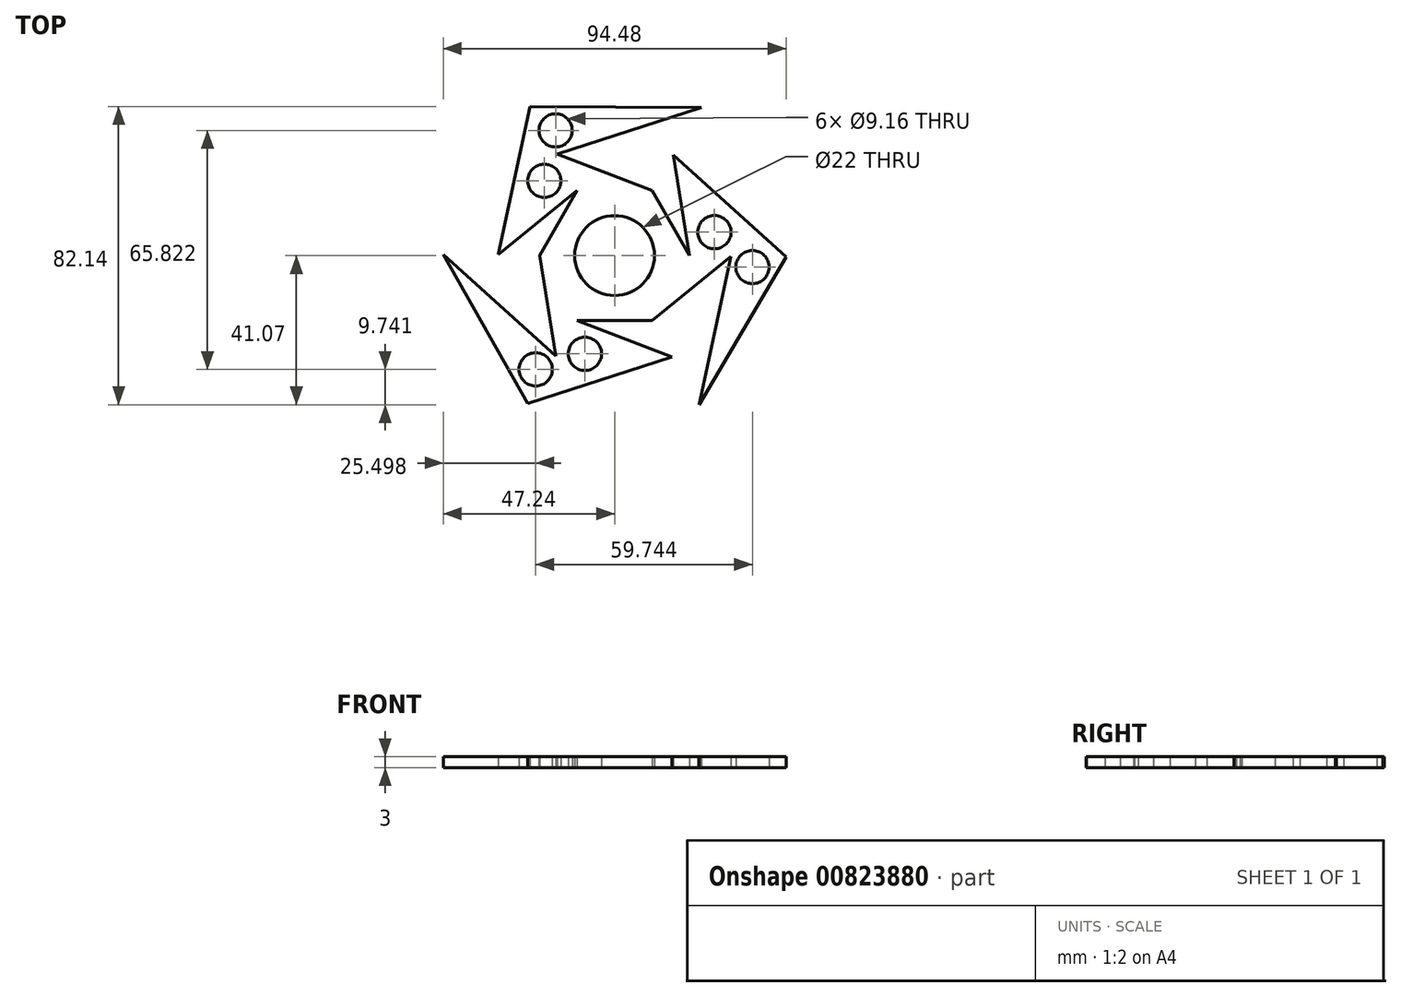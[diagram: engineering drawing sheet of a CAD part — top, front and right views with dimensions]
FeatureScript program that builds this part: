
annotation { "Feature Type Name" : "Feature", "Feature Type Description" : "" }
export const myFeature = defineFeature(function(context is Context, id is Id, definition is map)
    precondition{}
    {
        {
            var Q0;
            Q0=qCreatedBy(makeId("Top.planeOp"),FACE);
            var sketch = newSketch(context, id + "F0", { "sketchPlane" : qUnion([Q0])});
            skLineSegment(sketch, "E0.0", {"start": v(10.34, -17.92) * mm, "end": v(-10.34, -17.92) * mm});
            skPoint(sketch, "E0.0.midPoint", {"position": v(0, -17.92) * mm});
            skPoint(sketch, "E1.0.midPoint", {"position": v(-24.18, -13.74) * mm});
            skLineSegment(sketch, "E2", {"start": v(-20.69, 0) * mm, "end": v(-16.24, -27.7) * mm});
            skLineSegment(sketch, "E3", {"start": v(-10.34, -17.92) * mm, "end": v(15.87, -27.92) * mm});
            skArc(sketch, "E4", {"start": v(-8.4, 0.06) * mm, "mid": v(-8.4, 0.03) * mm, "end": v(-8.4, 0) * mm});
            skPoint(sketch, "E5.0.midPoint", {"position": v(15.87, -27.92) * mm});
            skLineSegment(sketch, "E6.1", {"start": v(-23.9, -40.75) * mm, "end": v(-47.24, 0.32) * mm});
            skPoint(sketch, "E6.0.midPoint", {"position": v(-0.28, -40.91) * mm});
            skLineSegment(sketch, "E7", {"start": v(15.87, -27.92) * mm, "end": v(-23.9, -40.75) * mm});
            skLineSegment(sketch, "E8", {"start": v(-16.24, -27.7) * mm, "end": v(-47.24, 0.32) * mm});
            skCircle(sketch, "E9", {"center": v(-8.17, -27.07) * mm, "radius": 4.58 * mm});
            skCircle(sketch, "E10", {"center": v(-21.74, -31.33) * mm, "radius": 4.58 * mm});
            skLineSegment(sketch, "E11.1.0", {"start": v(10.34, -17.92) * mm, "end": v(32.11, -0.22) * mm});
            skLineSegment(sketch, "E11.1.1", {"start": v(47.24, -0.32) * mm, "end": v(23.34, -41.07) * mm});
            skArc(sketch, "E11.1.2", {"start": v(4.15, -7.3) * mm, "mid": v(4.17, -7.29) * mm, "end": v(4.2, -7.27) * mm});
            skLineSegment(sketch, "E11.1.3", {"start": v(10.34, 17.92) * mm, "end": v(20.69, 0) * mm});
            skPoint(sketch, "E11.1.4", {"position": v(23.99, -14.07) * mm});
            skCircle(sketch, "E11.1.5", {"center": v(27.53, 6.46) * mm, "radius": 4.58 * mm});
            skPoint(sketch, "E11.1.6", {"position": v(16.24, 27.7) * mm});
            skPoint(sketch, "E11.1.7", {"position": v(15.52, 8.96) * mm});
            skCircle(sketch, "E11.1.8", {"center": v(38, -3.16) * mm, "radius": 4.58 * mm});
            skPoint(sketch, "E11.1.9", {"position": v(35.57, 20.22) * mm});
            skLineSegment(sketch, "E11.1.10", {"start": v(16.24, 27.7) * mm, "end": v(47.24, -0.32) * mm});
            skLineSegment(sketch, "E11.1.11", {"start": v(32.11, -0.22) * mm, "end": v(23.34, -41.07) * mm});
            skLineSegment(sketch, "E11.1.12", {"start": v(20.69, 0) * mm, "end": v(16.24, 27.7) * mm});
            skLineSegment(sketch, "E11.2.0", {"start": v(10.34, 17.92) * mm, "end": v(-15.87, 27.92) * mm});
            skLineSegment(sketch, "E11.2.1", {"start": v(-23.34, 41.07) * mm, "end": v(23.9, 40.75) * mm});
            skArc(sketch, "E11.2.2", {"start": v(4.25, 7.24) * mm, "mid": v(4.22, 7.26) * mm, "end": v(4.2, 7.27) * mm});
            skLineSegment(sketch, "E11.2.3", {"start": v(-20.69, 0) * mm, "end": v(-10.34, 17.92) * mm});
            skPoint(sketch, "E11.2.4", {"position": v(0.19, 27.8) * mm});
            skCircle(sketch, "E11.2.5", {"center": v(-19.35, 20.6) * mm, "radius": 4.58 * mm});
            skPoint(sketch, "E11.2.6", {"position": v(-32.11, 0.22) * mm});
            skPoint(sketch, "E11.2.7", {"position": v(-15.52, 8.96) * mm});
            skCircle(sketch, "E11.2.8", {"center": v(-16.26, 34.5) * mm, "radius": 4.58 * mm});
            skPoint(sketch, "E11.2.9", {"position": v(-35.3, 20.7) * mm});
            skLineSegment(sketch, "E11.2.10", {"start": v(-32.11, 0.22) * mm, "end": v(-23.34, 41.07) * mm});
            skLineSegment(sketch, "E11.2.11", {"start": v(-15.87, 27.92) * mm, "end": v(23.9, 40.75) * mm});
            skLineSegment(sketch, "E11.2.12", {"start": v(-10.34, 17.92) * mm, "end": v(-32.11, 0.22) * mm});
            skCircle(sketch, "E12", {"center": v(0, 0) * mm, "radius": 11 * mm});
            skSolve(sketch);
        }
        {
            var Q0;
            Q0 = qSketchRegion(id + "F0", true);
            extrude(context, id + "F1", {"entities" : qUnion([Q0]), "depth" : 3 * mm, "offsetDistance" : 25 * mm});
        }
    });
